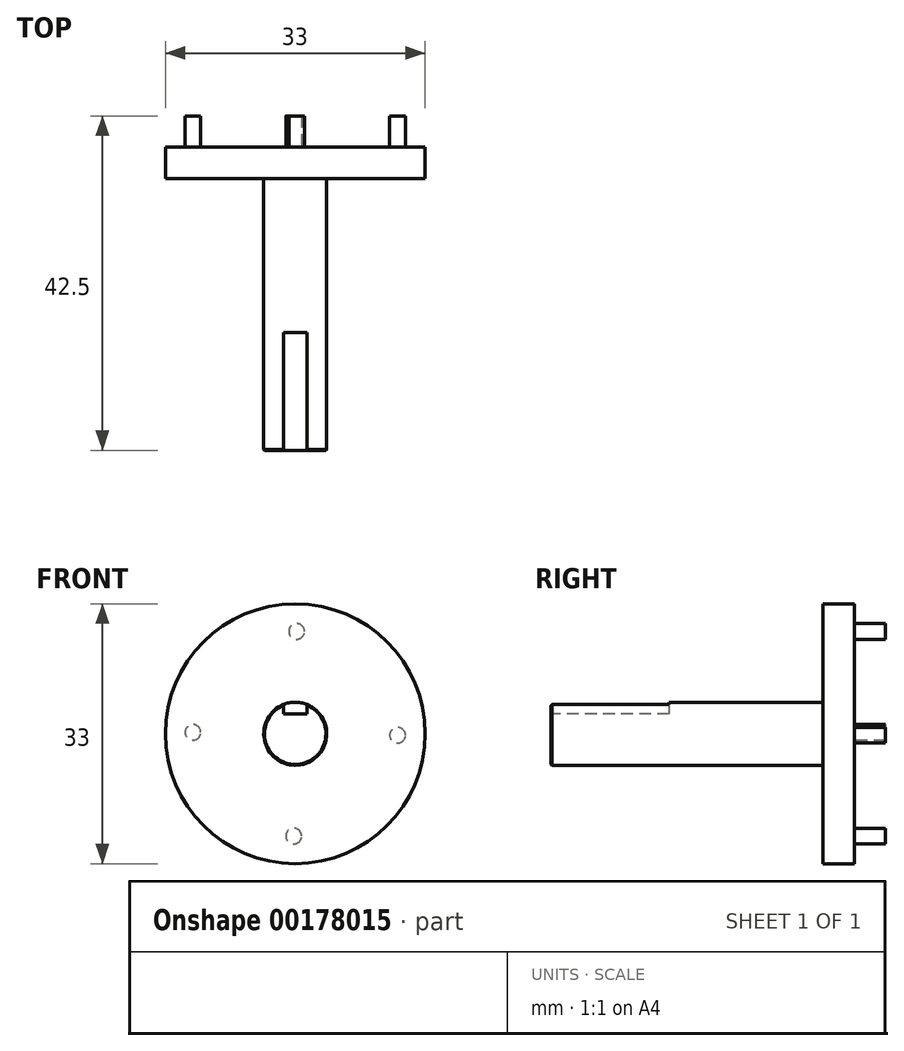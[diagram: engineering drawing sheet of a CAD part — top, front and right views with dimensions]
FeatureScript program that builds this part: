
annotation { "Feature Type Name" : "Feature", "Feature Type Description" : "" }
export const myFeature = defineFeature(function(context is Context, id is Id, definition is map)
    precondition{}
    {
        {
            var Q0;
            Q0=qCreatedBy(makeId("Front.planeOp"),FACE);
            var sketch = newSketch(context, id + "F0", { "sketchPlane" : qUnion([Q0])});
            skCircle(sketch, "E0", {"center": v(0, 0) * mm, "radius": 4 * mm});
            skSolve(sketch);
        }
        {
            var Q0;
            Q0=qSketchRegion(id+"F0",true);
            extrude(context, id + "F1", {"entities" : qUnion([Q0]), "oppositeDirection" : true, "depth" : 34.5 * mm});
        }
        {
            var Q0;
            Q0=qCreatedBy(makeId("Front.planeOp"),FACE);
            var sketch = newSketch(context, id + "F2", { "sketchPlane" : qUnion([Q0])});
            skLineSegment(sketch, "E1.bottom", {"start": v(-1.5, 4) * mm, "end": v(1.5, 4) * mm});
            skLineSegment(sketch, "E1.top", {"start": v(-1.5, 2.5) * mm, "end": v(1.5, 2.5) * mm});
            skLineSegment(sketch, "E1.left", {"start": v(-1.5, 4) * mm, "end": v(-1.5, 2.5) * mm});
            skLineSegment(sketch, "E1.right", {"start": v(1.5, 4) * mm, "end": v(1.5, 2.5) * mm});
            skSolve(sketch);
        }
        {
            var Q0;
            Q0=makeQuery(id+"F1.opExtrude","CAP_EDGE",EDGE,{"disambiguationData":[OSD([sQuery(id+"F0.wireOp",EDGE,"E0")])],"isStart":true});
            chamfer(context, id + "F3", {"entities" : qUnion([Q0]), "width" : 0.1 * mm, "tangentPropagation" : true});
        }
        {
            var Q0;
            Q0=qSketchRegion(id+"F2",true);
            extrude(context, id + "F4", {"entities" : qUnion([Q0]), "operationType" : NewBodyOperationType.REMOVE, "oppositeDirection" : true, "depth" : 15 * mm});
        }
        {
            var Q0;
            Q0=makeQuery(id+"F1.opExtrude","CAP_FACE",FACE,{"disambiguationData":[OSD([sQuery(id+"F0.wireOp",EDGE,"E0")])],"isStart":false});
            var sketch = newSketch(context, id + "F5", { "sketchPlane" : qUnion([Q0])});
            skCircle(sketch, "E2", {"center": v(0, 0) * mm, "radius": 16.5 * mm});
            skSolve(sketch);
        }
        {
            var Q0;
            Q0=qSketchRegion(id+"F5",true);
            extrude(context, id + "F6", {"entities" : qUnion([Q0]), "operationType" : NewBodyOperationType.ADD, "depth" : 4 * mm});
        }
        {
            var Q0;
            Q0=makeQuery(id+"F6.opExtrude","CAP_FACE",FACE,{"disambiguationData":[OSD([sQuery(id+"F5.wireOp",EDGE,"E2")])],"isStart":false});
            var sketch = newSketch(context, id + "F7", { "sketchPlane" : qUnion([Q0])});
            skPoint(sketch, "E3", {"position": v(0, 0) * mm});
            skCircle(sketch, "E4", {"center": v(-0.19, 13) * mm, "radius": 1 * mm});
            skCircle(sketch, "E5.1.0", {"center": v(-13, -0.19) * mm, "radius": 1 * mm});
            skCircle(sketch, "E5.2.0", {"center": v(0.19, -13) * mm, "radius": 1 * mm});
            skCircle(sketch, "E5.3.0", {"center": v(13, 0.19) * mm, "radius": 1 * mm});
            skSolve(sketch);
        }
        {
            var Q0;
            Q0=qSketchRegion(id+"F7",true);
            extrude(context, id + "F8", {"entities" : qUnion([Q0]), "operationType" : NewBodyOperationType.ADD, "depth" : 4 * mm});
        }
    });
